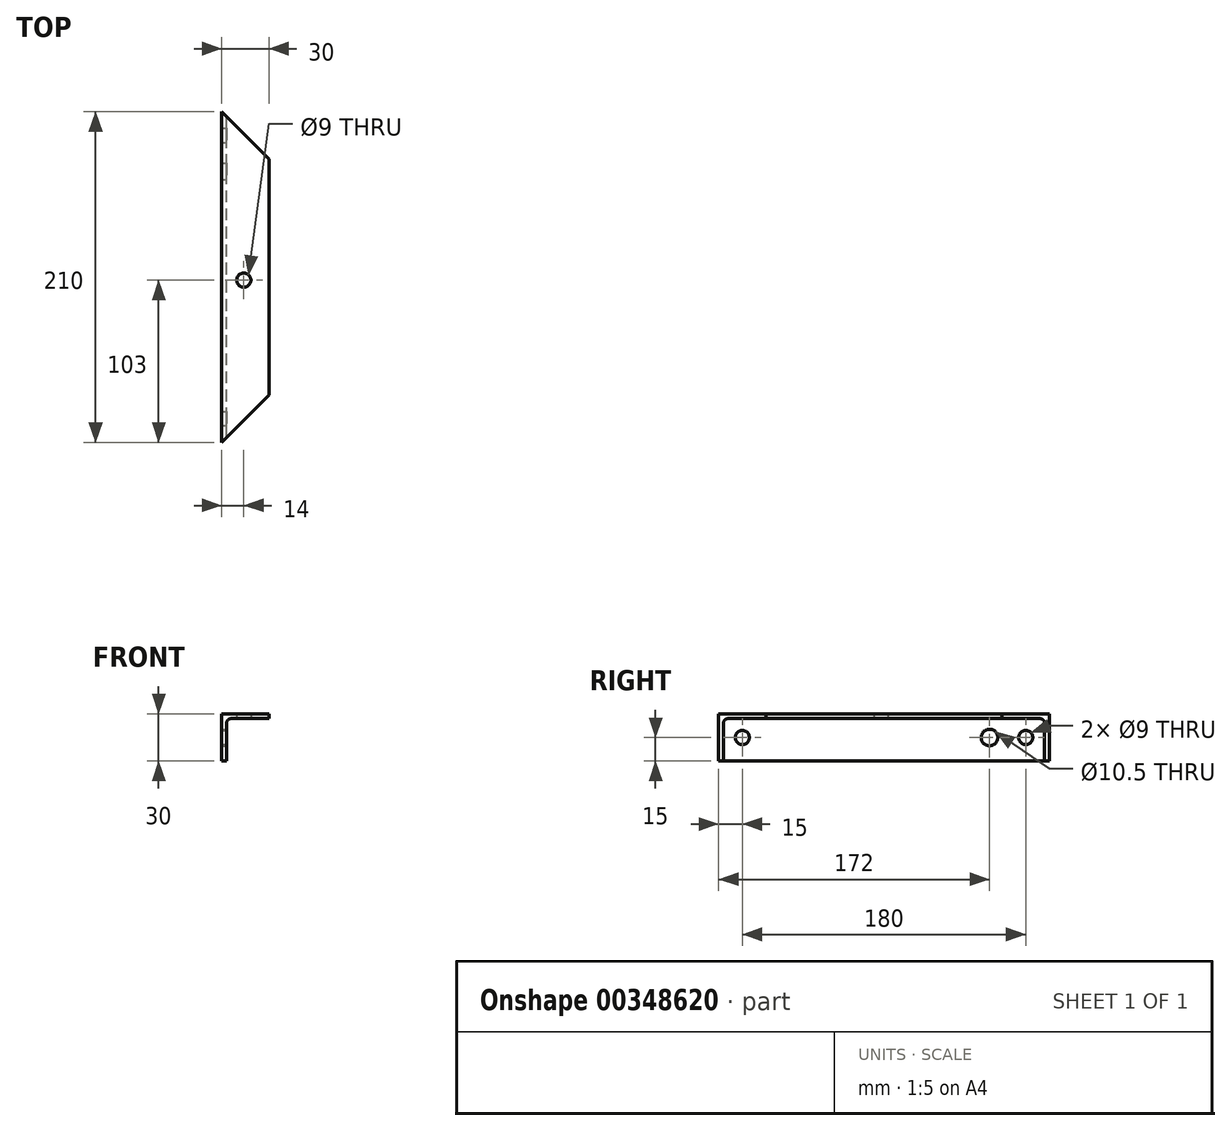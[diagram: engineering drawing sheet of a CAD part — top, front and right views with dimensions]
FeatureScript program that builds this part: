
annotation { "Feature Type Name" : "Feature", "Feature Type Description" : "" }
export const myFeature = defineFeature(function(context is Context, id is Id, definition is map)
    precondition{}
    {
        {
            var Q0;
            Q0=qCreatedBy(makeId("Front.planeOp"),FACE);
            var sketch = newSketch(context, id + "F0", { "sketchPlane" : qUnion([Q0])});
            skLineSegment(sketch, "E0", {"start": v(0, 0) * mm, "end": v(0, 30) * mm});
            skLineSegment(sketch, "E1", {"start": v(0, 30) * mm, "end": v(30, 30) * mm});
            skLineSegment(sketch, "E2", {"start": v(30, 30) * mm, "end": v(30, 27) * mm});
            skLineSegment(sketch, "E3", {"start": v(30, 27) * mm, "end": v(6, 27) * mm});
            skLineSegment(sketch, "E4", {"start": v(3, 24) * mm, "end": v(3, 0) * mm});
            skLineSegment(sketch, "E5", {"start": v(3, 0) * mm, "end": v(0, 0) * mm});
            skPoint(sketch, "E6.visualSharp", {"position": v(3, 27) * mm});
            skArc(sketch, "E6.filletArc", {"start": v(6, 27) * mm, "mid": v(3.88, 26.12) * mm, "end": v(3, 24) * mm});
            skSolve(sketch);
        }
        {
            var Q0;
            Q0=makeQuery(id+"F0.imprint","IMPRINT",FACE,{"disambiguationData":[TD([[makeQuery(id+"F0.imprint","IMPRINT",EDGE,{"derivedFrom":sQuery(id+"F0.wireOp",EDGE,"E0")}),-1.0]])]});
            extrude(context, id + "F1", {"entities" : qUnion([Q0]), "depth" : 210 * mm});
        }
        {
            var Q0;
            Q0=makeQuery(id+"F1.opExtrude","SWEPT_FACE",FACE,{"disambiguationData":[OSD([sQuery(id+"F0.wireOp",EDGE,"E4")])]});
            var sketch = newSketch(context, id + "F2", { "sketchPlane" : qUnion([Q0])});
            skPoint(sketch, "E7", {"position": v(-195, 15) * mm});
            skPoint(sketch, "E8", {"position": v(-15, 15) * mm});
            skSolve(sketch);
        }
        {
            var Q0;
            Q0=sQuery(id+"F2.wireOp",VERTEX,"E7");
            var Q1;
            Q1=sQuery(id+"F2.wireOp",VERTEX,"E8");
            var Q2;
            Q2=makeQuery(id+"F1.opExtrude","SWEPT_BODY",BODY,{"disambiguationData":[OSD([sQuery(id+"F0.wireOp",EDGE,"E0"),sQuery(id+"F0.wireOp",EDGE,"E1"),sQuery(id+"F0.wireOp",EDGE,"E2"),sQuery(id+"F0.wireOp",EDGE,"E3"),sQuery(id+"F0.wireOp",EDGE,"E4"),sQuery(id+"F0.wireOp",EDGE,"E5"),sQuery(id+"F0.wireOp",EDGE,"E6.filletArc")])]});
            hole(context, id + "F3", {"style" : HoleStyle.SIMPLE, "endStyle" : HoleEndStyle.BLIND, "holeDiameter" : 9 * mm, "holeDepth" : 12 * mm, "isTappedThrough" : true, "tappedDepth" : 12 * mm, "tapClearance" : 3, "locations" : qUnion([Q0, Q1]), "scope" : qUnion([Q2])});
        }
        {
            var Q0;
            Q0=makeQuery(id+"F1.opExtrude","SWEPT_FACE",FACE,{"disambiguationData":[OSD([sQuery(id+"F0.wireOp",EDGE,"E4")])]});
            var sketch = newSketch(context, id + "F4", { "sketchPlane" : qUnion([Q0])});
            skPoint(sketch, "E9", {"position": v(-38, 15) * mm});
            skLineSegment(sketch, "E10", {"start": v(-15, 15) * mm, "end": v(-38, 15) * mm, "construction": true});
            skSolve(sketch);
        }
        {
            var Q0;
            Q0=sQuery(id+"F4.wireOp",VERTEX,"E9");
            var Q1;
            Q1=makeQuery(id+"F1.opExtrude","SWEPT_BODY",BODY,{"disambiguationData":[OSD([sQuery(id+"F0.wireOp",EDGE,"E0"),sQuery(id+"F0.wireOp",EDGE,"E1"),sQuery(id+"F0.wireOp",EDGE,"E2"),sQuery(id+"F0.wireOp",EDGE,"E3"),sQuery(id+"F0.wireOp",EDGE,"E4"),sQuery(id+"F0.wireOp",EDGE,"E5"),sQuery(id+"F0.wireOp",EDGE,"E6.filletArc")])]});
            hole(context, id + "F5", {"style" : HoleStyle.SIMPLE, "endStyle" : HoleEndStyle.BLIND, "holeDiameter" : 10.5 * mm, "holeDepth" : 12 * mm, "isTappedThrough" : true, "tappedDepth" : 12 * mm, "tapClearance" : 3, "locations" : qUnion([Q0]), "scope" : qUnion([Q1])});
        }
        {
            var Q0;
            Q0=makeQuery(id+"F1.opExtrude","SWEPT_FACE",FACE,{"disambiguationData":[OSD([sQuery(id+"F0.wireOp",EDGE,"E3")])]});
            var sketch = newSketch(context, id + "F6", { "sketchPlane" : qUnion([Q0])});
            skPoint(sketch, "E11", {"position": v(14, 107) * mm});
            skSolve(sketch);
        }
        {
            var Q0;
            Q0=sQuery(id+"F6.wireOp",VERTEX,"E11");
            var Q1;
            Q1=makeQuery(id+"F1.opExtrude","SWEPT_BODY",BODY,{"disambiguationData":[OSD([sQuery(id+"F0.wireOp",EDGE,"E0"),sQuery(id+"F0.wireOp",EDGE,"E1"),sQuery(id+"F0.wireOp",EDGE,"E2"),sQuery(id+"F0.wireOp",EDGE,"E3"),sQuery(id+"F0.wireOp",EDGE,"E4"),sQuery(id+"F0.wireOp",EDGE,"E5"),sQuery(id+"F0.wireOp",EDGE,"E6.filletArc")])]});
            hole(context, id + "F7", {"style" : HoleStyle.SIMPLE, "endStyle" : HoleEndStyle.BLIND, "holeDiameter" : 9 * mm, "holeDepth" : 12 * mm, "isTappedThrough" : true, "tappedDepth" : 12 * mm, "tapClearance" : 3, "locations" : qUnion([Q0]), "scope" : qUnion([Q1])});
        }
        {
            var Q0;
            Q0=makeQuery(id+"F1.opExtrude","SWEPT_FACE",FACE,{"disambiguationData":[OSD([sQuery(id+"F0.wireOp",EDGE,"E5")])]});
            var sketch = newSketch(context, id + "F8", { "sketchPlane" : qUnion([Q0])});
            skLineSegment(sketch, "E12", {"start": v(0, 210) * mm, "end": v(30, 180) * mm});
            skLineSegment(sketch, "E13", {"start": v(0, 0) * mm, "end": v(30, 30) * mm});
            skLineSegment(sketch, "E14", {"start": v(30, 30) * mm, "end": v(30, 0) * mm});
            skLineSegment(sketch, "E15", {"start": v(30, 0) * mm, "end": v(0, 0) * mm});
            skLineSegment(sketch, "E16", {"start": v(30, 180) * mm, "end": v(30, 210) * mm});
            skLineSegment(sketch, "E17", {"start": v(30, 210) * mm, "end": v(0, 210) * mm});
            skSolve(sketch);
        }
        {
            var Q0;
            {var subQ0=sQuery(id+"F8.wireOp",EDGE,"E14");Q0=makeQuery(id+"F8.imprint","IMPRINT",FACE,{"disambiguationData":[TD([[makeQuery(id+"F8.imprint","IMPRINT",EDGE,{"derivedFrom":subQ0}),-1.0]])]});}
            var Q1;
            {var subQ0=sQuery(id+"F8.wireOp",EDGE,"E16");Q1=makeQuery(id+"F8.imprint","IMPRINT",FACE,{"disambiguationData":[TD([[makeQuery(id+"F8.imprint","IMPRINT",EDGE,{"derivedFrom":subQ0}),1.0]])]});}
            var Q2;
            {var subQ1=sQuery(id+"F8.wireOp",EDGE,"E13");var subQ2=sQuery(id+"F0.wireOp",EDGE,"E5");var subQ4=makeQuery(id+"F1.opExtrude","SWEPT_EDGE",EDGE,{"disambiguationData":[OSD([sQuery(id+"F0.wireOp",EDGE,"E4"),subQ2])]});var subQ5=makeQuery(id+"F8.imprint","INTERSECT",VERTEX,{"derivedFrom":[subQ4,subQ1]});Q2=makeQuery(id+"F8.imprint","IMPRINT",FACE,{"disambiguationData":[TD([[makeQuery(id+"F8.imprint","IMPRINT",EDGE,{"disambiguationData":[TD([[subQ5,1.0]])],"derivedFrom":subQ1}),-1.0]])]});}
            var Q3;
            {var subQ1=sQuery(id+"F8.wireOp",EDGE,"E12");var subQ2=sQuery(id+"F0.wireOp",EDGE,"E5");var subQ4=makeQuery(id+"F1.opExtrude","SWEPT_EDGE",EDGE,{"disambiguationData":[OSD([sQuery(id+"F0.wireOp",EDGE,"E4"),subQ2])]});var subQ5=makeQuery(id+"F8.imprint","INTERSECT",VERTEX,{"derivedFrom":[subQ4,subQ1]});Q3=makeQuery(id+"F8.imprint","IMPRINT",FACE,{"disambiguationData":[TD([[makeQuery(id+"F8.imprint","IMPRINT",EDGE,{"disambiguationData":[TD([[subQ5,1.0]])],"derivedFrom":subQ1}),1.0]])]});}
            extrude(context, id + "F9", {"entities" : qUnion([Q0, Q1, Q2, Q3]), "operationType" : NewBodyOperationType.REMOVE, "oppositeDirection" : true, "depth" : 94 * mm});
        }
    });
